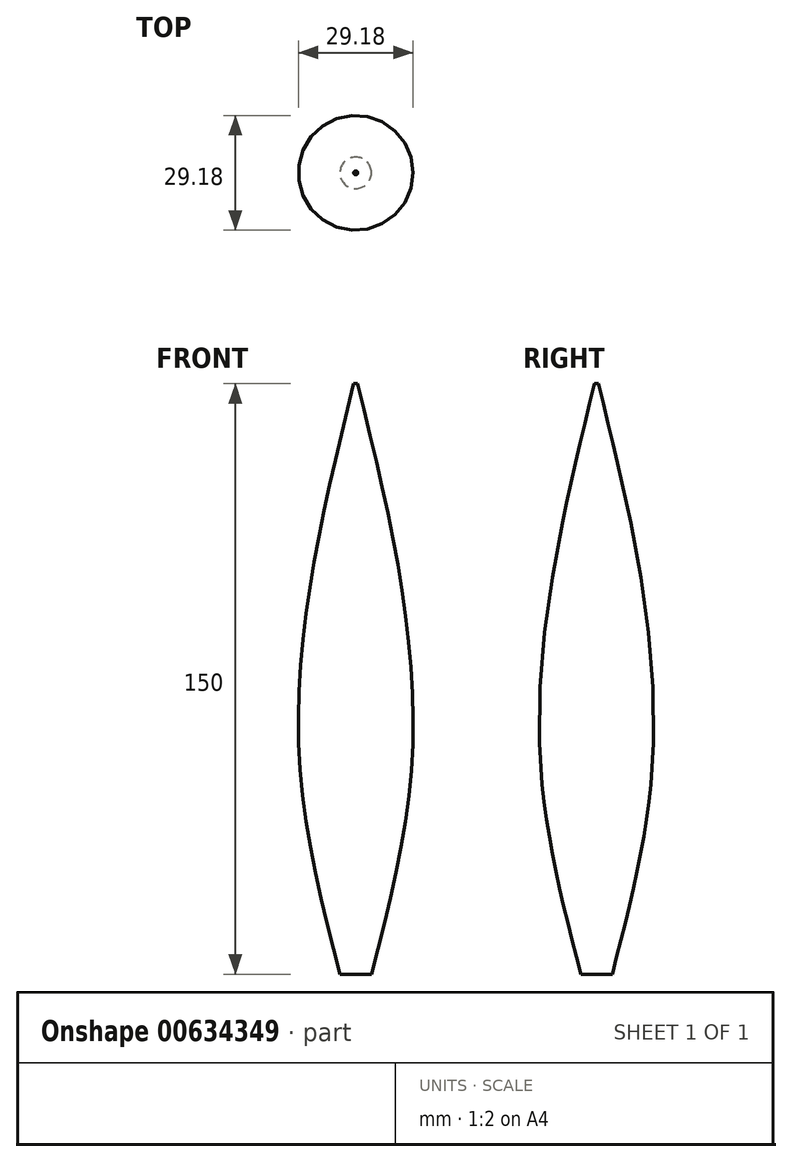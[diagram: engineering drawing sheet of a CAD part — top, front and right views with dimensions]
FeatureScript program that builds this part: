
annotation { "Feature Type Name" : "Feature", "Feature Type Description" : "" }
export const myFeature = defineFeature(function(context is Context, id is Id, definition is map)
    precondition{}
    {
        {
            var Q0;
            Q0=qCreatedBy(makeId("Top.planeOp"),FACE);
            cPlane(context, id + "F0", {"entities" : qUnion([Q0]), "cplaneType" : CPlaneType.OFFSET, "offset" : 50 * mm, "width" : 150 * mm, "height" : 150 * mm});
        }
        {
            var Q0;
            Q0=qCreatedBy(makeId("Top.planeOp"),FACE);
            cPlane(context, id + "F1", {"entities" : qUnion([Q0]), "cplaneType" : CPlaneType.OFFSET, "offset" : 150 * mm, "width" : 150 * mm, "height" : 150 * mm});
        }
        {
            var Q0;
            Q0=qCreatedBy(id+"F1.planeOp",FACE);
            var sketch = newSketch(context, id + "F2", { "sketchPlane" : qUnion([Q0])});
            skCircle(sketch, "E0", {"center": v(0, 0) * mm, "radius": 0.5 * mm});
            skSolve(sketch);
        }
        {
            var Q0;
            Q0=qCreatedBy(id+"F0.planeOp",FACE);
            var sketch = newSketch(context, id + "F3", { "sketchPlane" : qUnion([Q0])});
            skCircle(sketch, "E1", {"center": v(0, 0) * mm, "radius": 14 * mm});
            skSolve(sketch);
        }
        {
            var Q0;
            Q0=qCreatedBy(makeId("Top.planeOp"),FACE);
            var sketch = newSketch(context, id + "F4", { "sketchPlane" : qUnion([Q0])});
            skCircle(sketch, "E2", {"center": v(0, 0) * mm, "radius": 4 * mm});
            skSolve(sketch);
        }
        {
            var Q0;
            Q0 = qSketchRegion(id + "F4", true);
            var Q1;
            Q1 = qSketchRegion(id + "F3", true);
            var Q2;
            Q2 = qSketchRegion(id + "F2", true);
            loft(context, id + "F5", {"sheetProfilesArray" : [{ "sheetProfileEntities" : qUnion([Q0]) }, { "sheetProfileEntities" : qUnion([Q1]) }, { "sheetProfileEntities" : qUnion([Q2]) }]});
        }
    });
